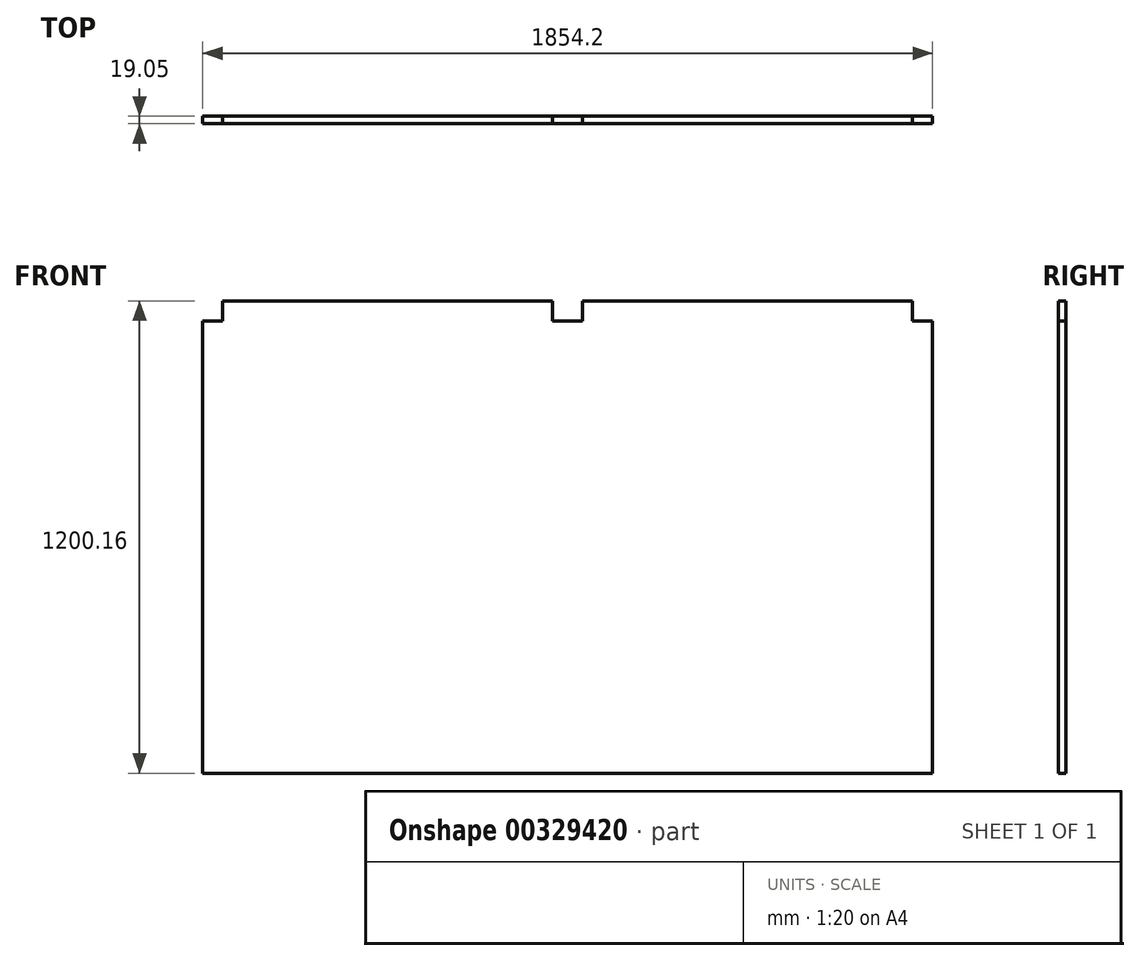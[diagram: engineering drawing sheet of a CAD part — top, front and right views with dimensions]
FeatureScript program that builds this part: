
annotation { "Feature Type Name" : "Feature", "Feature Type Description" : "" }
export const myFeature = defineFeature(function(context is Context, id is Id, definition is map)
    precondition{}
    {
        {
            var Q0;
            Q0=qCreatedBy(makeId("Front.planeOp"),FACE);
            var sketch = newSketch(context, id + "F0", { "sketchPlane" : qUnion([Q0])});
            skLineSegment(sketch, "E0.bottom", {"start": v(927.1, -600.07) * mm, "end": v(-927.1, -600.08) * mm});
            skLineSegment(sketch, "E0.top", {"start": v(876.3, 600.08) * mm, "end": v(38.1, 600.07) * mm});
            skLineSegment(sketch, "E0.left", {"start": v(927.1, -600.07) * mm, "end": v(927.1, 549.28) * mm});
            skLineSegment(sketch, "E0.right", {"start": v(-927.1, -600.08) * mm, "end": v(-927.1, 549.28) * mm});
            skPoint(sketch, "E0.middle", {"position": v(0, 0) * mm});
            skLineSegment(sketch, "E1.top", {"start": v(-927.1, 549.28) * mm, "end": v(-876.3, 549.28) * mm});
            skLineSegment(sketch, "E1.right", {"start": v(-876.3, 600.08) * mm, "end": v(-876.3, 549.28) * mm});
            skPoint(sketch, "E2.orphan", {"position": v(-927.1, 600.07) * mm});
            skPoint(sketch, "E3.MirrorP", {"position": v(927.1, 600.07) * mm});
            skLineSegment(sketch, "E4.MirrorCS", {"start": v(876.3, 600.08) * mm, "end": v(876.3, 549.28) * mm});
            skLineSegment(sketch, "E5.MirrorCS", {"start": v(927.1, 549.28) * mm, "end": v(876.3, 549.28) * mm});
            skPoint(sketch, "E6.orphan", {"position": v(927.1, 600.08) * mm});
            skLineSegment(sketch, "E7", {"start": v(0, 0) * mm, "end": v(0, 600.07) * mm, "construction": true});
            skLineSegment(sketch, "E8.bottom", {"start": v(38.1, 549.28) * mm, "end": v(-38.1, 549.27) * mm});
            skLineSegment(sketch, "E8.left", {"start": v(38.1, 549.27) * mm, "end": v(38.1, 600.08) * mm});
            skLineSegment(sketch, "E8.right", {"start": v(-38.1, 549.27) * mm, "end": v(-38.1, 600.08) * mm});
            skPoint(sketch, "E8.middle", {"position": v(0, 600.07) * mm});
            skPoint(sketch, "E9.orphan", {"position": v(-38.1, 650.88) * mm});
            skPoint(sketch, "E10.orphan", {"position": v(38.1, 650.88) * mm});
            skLineSegment(sketch, "E11.trimOffspring", {"start": v(-38.1, 600.07) * mm, "end": v(-876.3, 600.07) * mm});
            skSolve(sketch);
        }
        {
            var Q0;
            Q0 = qSketchRegion(id + "F0", true);
            extrude(context, id + "F1", {"entities" : qUnion([Q0]), "depth" : 19.05 * mm});
        }
    });
